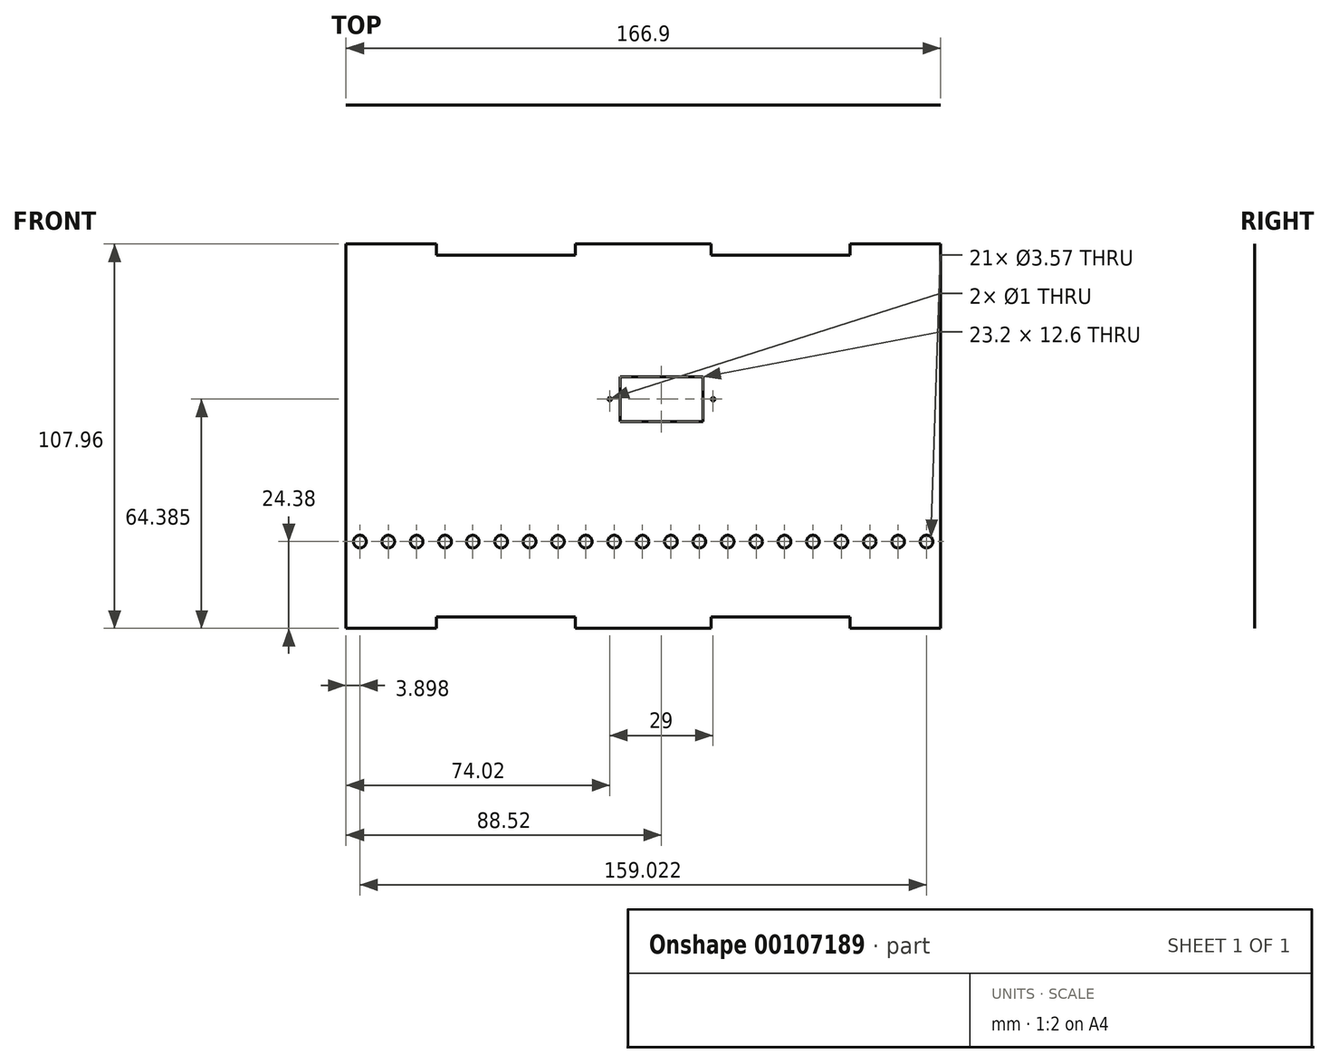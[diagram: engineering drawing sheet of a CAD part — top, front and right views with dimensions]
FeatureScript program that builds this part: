
annotation { "Feature Type Name" : "Feature", "Feature Type Description" : "" }
export const myFeature = defineFeature(function(context is Context, id is Id, definition is map)
    precondition{}
    {
        {
            var Q0;
            Q0=qCreatedBy(makeId("Front.planeOp"),FACE);
            var sketch = newSketch(context, id + "F0", { "sketchPlane" : qUnion([Q0])});
            skPoint(sketch, "E0.middle", {"position": v(0, 0) * mm});
            skCircle(sketch, "E1", {"center": v(0, 0) * mm, "radius": 1.79 * mm});
            skCircle(sketch, "E2.1.0.0", {"center": v(7.97, 0) * mm, "radius": 1.79 * mm});
            skCircle(sketch, "E2.2.0.0", {"center": v(15.94, 0) * mm, "radius": 1.79 * mm});
            skCircle(sketch, "E2.3.0.0", {"center": v(23.91, 0) * mm, "radius": 1.79 * mm});
            skCircle(sketch, "E2.4.0.0", {"center": v(31.88, 0) * mm, "radius": 1.79 * mm});
            skCircle(sketch, "E2.5.0.0", {"center": v(39.85, 0) * mm, "radius": 1.79 * mm});
            skCircle(sketch, "E2.6.0.0", {"center": v(47.82, 0) * mm, "radius": 1.79 * mm});
            skCircle(sketch, "E2.7.0.0", {"center": v(55.8, 0) * mm, "radius": 1.79 * mm});
            skCircle(sketch, "E2.8.0.0", {"center": v(63.76, 0) * mm, "radius": 1.79 * mm});
            skCircle(sketch, "E2.9.0.0", {"center": v(71.73, 0) * mm, "radius": 1.79 * mm});
            skLineSegment(sketch, "E2.direction1", {"start": v(1.79, 0) * mm, "end": v(7.97, 0) * mm, "construction": true});
            skCircle(sketch, "E3.MirrorC", {"center": v(-7.8, 0) * mm, "radius": 1.79 * mm});
            skCircle(sketch, "E4.MirrorC", {"center": v(-15.76, 0) * mm, "radius": 1.79 * mm});
            skCircle(sketch, "E5.MirrorC", {"center": v(-23.73, 0) * mm, "radius": 1.79 * mm});
            skCircle(sketch, "E6.MirrorC", {"center": v(-31.7, 0) * mm, "radius": 1.79 * mm});
            skCircle(sketch, "E7.MirrorC", {"center": v(-63.38, 0) * mm, "radius": 1.79 * mm});
            skCircle(sketch, "E8.MirrorC", {"center": v(-47.44, 0) * mm, "radius": 1.79 * mm});
            skCircle(sketch, "E9.MirrorC", {"center": v(-55.41, 0) * mm, "radius": 1.79 * mm});
            skCircle(sketch, "E10.MirrorC", {"center": v(-39.47, 0) * mm, "radius": 1.79 * mm});
            skLineSegment(sketch, "E11", {"start": v(-67.28, -21.2) * mm, "end": v(-67.28, 57.32) * mm});
            skPoint(sketch, "E11.startSnap0", {"position": v(-67.28, 5.4) * mm});
            skPoint(sketch, "E11.endSnap0", {"position": v(-67.28, 29.6) * mm});
            skLineSegment(sketch, "E12", {"start": v(-67.28, 80.4) * mm, "end": v(-67.28, 57.32) * mm});
            skLineSegment(sketch, "E13.bottom", {"start": v(99.63, 80.4) * mm, "end": v(74.23, 80.4) * mm});
            skLineSegment(sketch, "E13.top", {"start": v(99.63, 83.58) * mm, "end": v(74.23, 83.58) * mm});
            skLineSegment(sketch, "E13.left", {"start": v(99.63, 80.4) * mm, "end": v(99.63, 83.58) * mm});
            skLineSegment(sketch, "E13.right", {"start": v(74.23, 80.4) * mm, "end": v(74.23, 83.58) * mm});
            skLineSegment(sketch, "E14.bottom", {"start": v(35.22, 80.4) * mm, "end": v(-2.88, 80.4) * mm});
            skLineSegment(sketch, "E14.top", {"start": v(35.22, 83.58) * mm, "end": v(-2.88, 83.58) * mm});
            skLineSegment(sketch, "E14.left", {"start": v(35.22, 80.4) * mm, "end": v(35.22, 83.58) * mm});
            skLineSegment(sketch, "E14.right", {"start": v(-2.88, 80.4) * mm, "end": v(-2.88, 83.58) * mm});
            skLineSegment(sketch, "E15.bottom", {"start": v(-67.28, 80.4) * mm, "end": v(-41.88, 80.4) * mm});
            skLineSegment(sketch, "E15.top", {"start": v(-67.28, 83.58) * mm, "end": v(-41.88, 83.58) * mm});
            skLineSegment(sketch, "E15.left", {"start": v(-67.28, 80.4) * mm, "end": v(-67.28, 83.58) * mm});
            skLineSegment(sketch, "E15.right", {"start": v(-41.88, 80.4) * mm, "end": v(-41.88, 83.58) * mm});
            skPoint(sketch, "E16", {"position": v(16.17, 80.4) * mm});
            skLineSegment(sketch, "E17.bottom", {"start": v(-67.28, -21.2) * mm, "end": v(-41.88, -21.2) * mm});
            skLineSegment(sketch, "E17.top", {"start": v(-67.28, -24.38) * mm, "end": v(-41.88, -24.38) * mm});
            skLineSegment(sketch, "E17.left", {"start": v(-67.28, -21.2) * mm, "end": v(-67.28, -24.38) * mm});
            skLineSegment(sketch, "E17.right", {"start": v(-41.88, -21.2) * mm, "end": v(-41.88, -24.38) * mm});
            skLineSegment(sketch, "E18.bottom", {"start": v(-2.88, -21.2) * mm, "end": v(35.22, -21.2) * mm});
            skLineSegment(sketch, "E18.top", {"start": v(-2.88, -24.38) * mm, "end": v(35.22, -24.38) * mm});
            skLineSegment(sketch, "E18.left", {"start": v(-2.88, -21.2) * mm, "end": v(-2.88, -24.38) * mm});
            skLineSegment(sketch, "E18.right", {"start": v(35.22, -21.2) * mm, "end": v(35.22, -24.38) * mm});
            skLineSegment(sketch, "E19.bottom", {"start": v(99.63, -21.2) * mm, "end": v(74.23, -21.2) * mm});
            skLineSegment(sketch, "E19.top", {"start": v(99.63, -24.38) * mm, "end": v(74.23, -24.38) * mm});
            skLineSegment(sketch, "E19.left", {"start": v(99.63, -21.2) * mm, "end": v(99.63, -24.38) * mm});
            skLineSegment(sketch, "E19.right", {"start": v(74.23, -21.2) * mm, "end": v(74.23, -24.38) * mm});
            skPoint(sketch, "E20", {"position": v(16.17, -21.2) * mm});
            skCircle(sketch, "E21.7.0.0", {"center": v(79.7, 0) * mm, "radius": 1.79 * mm});
            skCircle(sketch, "E22.7.0.0", {"center": v(87.67, 0) * mm, "radius": 1.79 * mm});
            skCircle(sketch, "E23.7.0.0", {"center": v(95.64, 0) * mm, "radius": 1.79 * mm});
            skLineSegment(sketch, "E24", {"start": v(99.63, -21.2) * mm, "end": v(99.63, 80.4) * mm});
            skPoint(sketch, "E24.startSnap0", {"position": v(99.63, 0) * mm});
            skLineSegment(sketch, "E25", {"start": v(-67.28, 80.4) * mm, "end": v(99.63, 80.4) * mm});
            skLineSegment(sketch, "E26", {"start": v(99.62, -21.2) * mm, "end": v(-67.28, -21.2) * mm});
            skLineSegment(sketch, "E27.bottom", {"start": v(9.64, 46.3) * mm, "end": v(32.84, 46.3) * mm});
            skLineSegment(sketch, "E27.top", {"start": v(9.64, 33.7) * mm, "end": v(32.84, 33.7) * mm});
            skLineSegment(sketch, "E27.left", {"start": v(9.64, 46.3) * mm, "end": v(9.64, 33.7) * mm});
            skLineSegment(sketch, "E27.right", {"start": v(32.84, 46.3) * mm, "end": v(32.84, 33.7) * mm});
            skPoint(sketch, "E28", {"position": v(15.94, 46.3) * mm});
            skPoint(sketch, "E29.startSnap0", {"position": v(21.24, 40) * mm});
            skCircle(sketch, "E30", {"center": v(35.74, 40) * mm, "radius": 0.5 * mm});
            skCircle(sketch, "E31", {"center": v(6.74, 40) * mm, "radius": 0.5 * mm});
            skCircle(sketch, "E32", {"center": v(15.94, 40) * mm, "radius": 6.3 * mm});
            skPoint(sketch, "E32.first.point", {"position": v(9.64, 40) * mm});
            skPoint(sketch, "E32.third.point", {"position": v(15.94, 33.7) * mm});
            skSolve(sketch);
        }
        {
            var Q0;
            Q0=makeQuery(id+"F0.imprint","IMPRINT",FACE,{"disambiguationData":[TD([[makeQuery(id+"F0.imprint","IMPRINT",EDGE,{"derivedFrom":sQuery(id+"F0.wireOp",EDGE,"E15.top")}),-1.0]])]});
            var Q1;
            Q1=makeQuery(id+"F0.imprint","IMPRINT",FACE,{"disambiguationData":[TD([[makeQuery(id+"F0.imprint","IMPRINT",EDGE,{"derivedFrom":sQuery(id+"F0.wireOp",EDGE,"E14.top")}),1.0]])]});
            var Q2;
            Q2=makeQuery(id+"F0.imprint","IMPRINT",FACE,{"disambiguationData":[TD([[makeQuery(id+"F0.imprint","IMPRINT",EDGE,{"derivedFrom":sQuery(id+"F0.wireOp",EDGE,"E13.top")}),1.0]])]});
            var Q3;
            Q3=makeQuery(id+"F0.imprint","IMPRINT",FACE,{"disambiguationData":[TD([[makeQuery(id+"F0.imprint","IMPRINT",EDGE,{"derivedFrom":sQuery(id+"F0.wireOp",EDGE,"E19.top")}),-1.0]])]});
            var Q4;
            Q4=makeQuery(id+"F0.imprint","IMPRINT",FACE,{"disambiguationData":[TD([[makeQuery(id+"F0.imprint","IMPRINT",EDGE,{"derivedFrom":sQuery(id+"F0.wireOp",EDGE,"E18.top")}),1.0]])]});
            var Q5;
            Q5=makeQuery(id+"F0.imprint","IMPRINT",FACE,{"disambiguationData":[TD([[makeQuery(id+"F0.imprint","IMPRINT",EDGE,{"derivedFrom":sQuery(id+"F0.wireOp",EDGE,"E17.top")}),1.0]])]});
            var Q6;
            Q6=makeQuery(id+"F0.imprint","IMPRINT",FACE,{"disambiguationData":[TD([[makeQuery(id+"F0.imprint","IMPRINT",EDGE,{"derivedFrom":sQuery(id+"F0.wireOp",EDGE,"E1")}),-1.0]])]});
            extrude(context, id + "F1", {"entities" : qUnion([Q0, Q1, Q2, Q3, Q4, Q5, Q6]), "depth" : 1 / 203.2 * mm});
        }
    });
